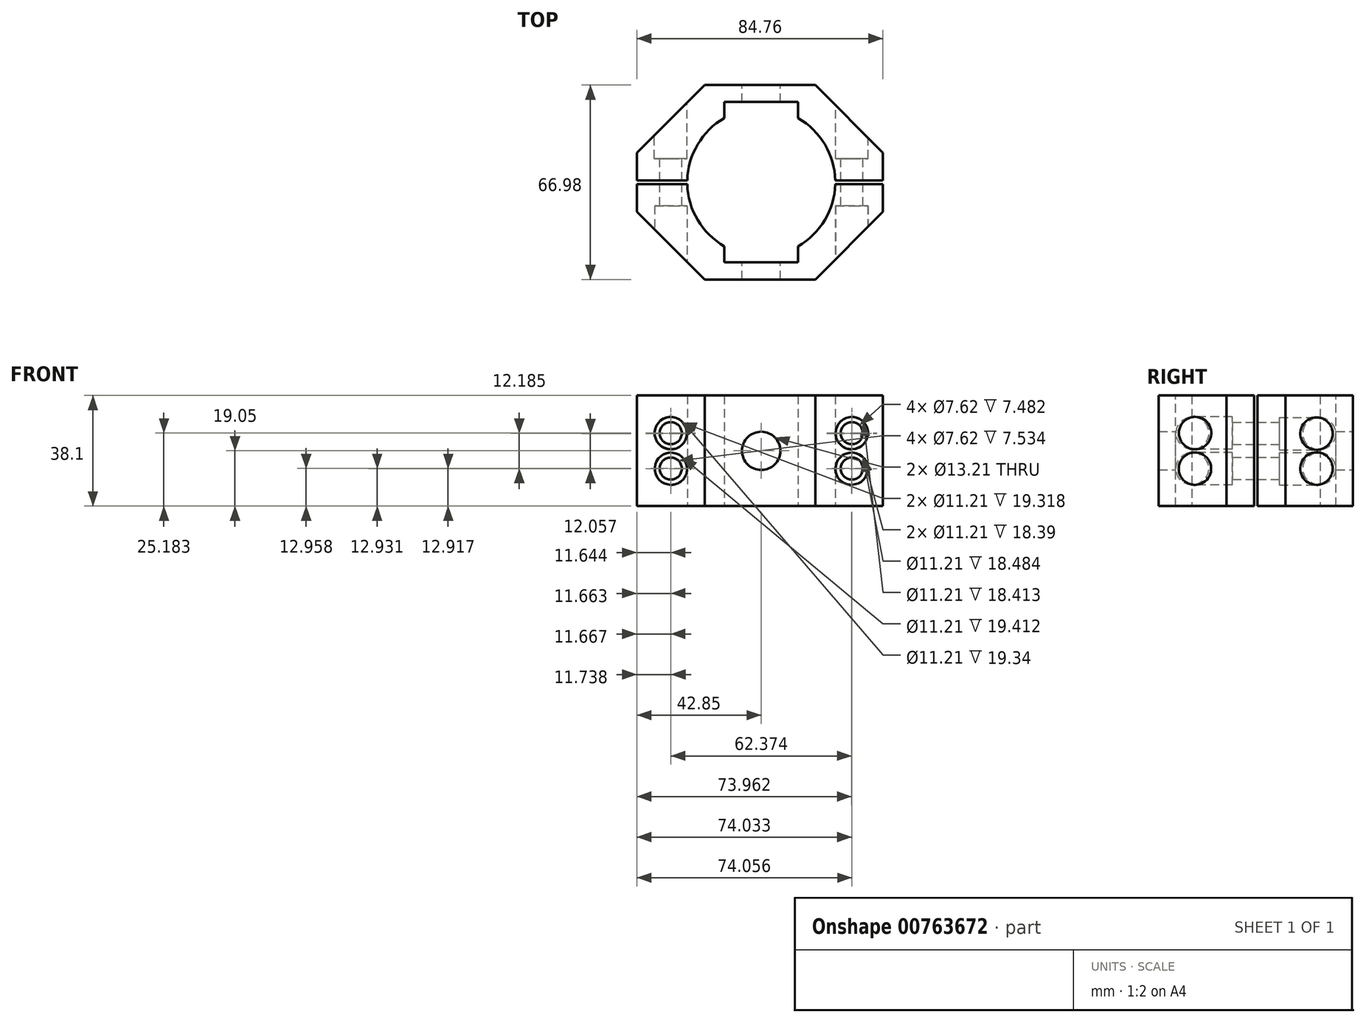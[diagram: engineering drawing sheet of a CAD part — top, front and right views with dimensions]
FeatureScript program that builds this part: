
annotation { "Feature Type Name" : "Feature", "Feature Type Description" : "" }
export const myFeature = defineFeature(function(context is Context, id is Id, definition is map)
    precondition{}
    {
        {
            var Q0;
            Q0=qCreatedBy(makeId("Top.planeOp"),FACE);
            var sketch = newSketch(context, id + "F0", { "sketchPlane" : qUnion([Q0])});
            skLineSegment(sketch, "E0", {"start": v(18.59, 33.5) * mm, "end": v(52.08, 0) * mm});
            skLineSegment(sketch, "E1", {"start": v(52.08, 0) * mm, "end": v(18.59, -33.5) * mm});
            skLineSegment(sketch, "E2", {"start": v(18.59, -33.5) * mm, "end": v(-19.51, -33.5) * mm});
            skLineSegment(sketch, "E3", {"start": v(-19.51, -33.5) * mm, "end": v(-53, 0) * mm});
            skLineSegment(sketch, "E4", {"start": v(-53, 0) * mm, "end": v(-19.51, 33.5) * mm});
            skCircle(sketch, "E5", {"center": v(0, 0) * mm, "radius": 25.48 * mm});
            skLineSegment(sketch, "E6", {"start": v(-19.51, 33.5) * mm, "end": v(18.59, 33.5) * mm});
            skLineSegment(sketch, "E7", {"start": v(0, 33.5) * mm, "end": v(0, 0) * mm});
            skLineSegment(sketch, "E8.bottom", {"start": v(-56.04, 16.89) * mm, "end": v(-42.85, 16.89) * mm});
            skLineSegment(sketch, "E8.top", {"start": v(-56.04, -17.81) * mm, "end": v(-42.85, -17.81) * mm});
            skLineSegment(sketch, "E8.left", {"start": v(-56.04, 16.89) * mm, "end": v(-56.04, -17.81) * mm});
            skLineSegment(sketch, "E8.right", {"start": v(-42.85, 16.89) * mm, "end": v(-42.85, -17.81) * mm});
            skLineSegment(sketch, "E9.left", {"start": v(41.9, 16.59) * mm, "end": v(41.9, -18.11) * mm});
            skLineSegment(sketch, "E9.bottom", {"start": v(41.9, 16.59) * mm, "end": v(54.8, 16.59) * mm});
            skLineSegment(sketch, "E9.right", {"start": v(54.8, 16.59) * mm, "end": v(54.8, -18.11) * mm});
            skLineSegment(sketch, "E9.top", {"start": v(41.9, -18.11) * mm, "end": v(54.8, -18.11) * mm});
            skLineSegment(sketch, "E10", {"start": v(-53, 0) * mm, "end": v(-42.85, 0) * mm});
            skLineSegment(sketch, "E11", {"start": v(41.92, 0) * mm, "end": v(52.08, 0) * mm});
            skSolve(sketch);
        }
        {
            var Q0;
            {var subQ13=sQuery(id+"F0.wireOp",EDGE,"E2");Q0=makeQuery(id+"F0.imprint","IMPRINT",FACE,{"disambiguationData":[TD([[makeQuery(id+"F0.imprint","IMPRINT",EDGE,{"derivedFrom":subQ13}),-1.0]])]});}
            extrude(context, id + "F1", {"entities" : qUnion([Q0]), "endBound" : BoundingType.SYMMETRIC, "depth" : 38.1 * mm});
        }
        {
            var Q0;
            Q0=makeQuery(id+"F1.opExtrude","SWEPT_FACE",FACE,{"disambiguationData":[OSD([sQuery(id+"F0.wireOp",EDGE,"E6")])]});
            var sketch = newSketch(context, id + "F2", { "sketchPlane" : qUnion([Q0])});
            skCircle(sketch, "E12.MirrorC", {"center": v(31.19, 6.1) * mm, "radius": 3.81 * mm});
            skCircle(sketch, "E13", {"center": v(-31.19, 6.1) * mm, "radius": 3.81 * mm});
            skCircle(sketch, "E14", {"center": v(-31.19, -6.1) * mm, "radius": 3.81 * mm});
            skCircle(sketch, "E15.MirrorC", {"center": v(31.19, -6.1) * mm, "radius": 3.81 * mm});
            skLineSegment(sketch, "E16", {"start": v(-31.19, 6.1) * mm, "end": v(-31.19, -6.1) * mm});
            skLineSegment(sketch, "E17", {"start": v(31.19, 6.1) * mm, "end": v(31.19, -6.1) * mm});
            skCircle(sketch, "E18", {"center": v(0, 0) * mm, "radius": 6.6 * mm});
            skLineSegment(sketch, "E19", {"start": v(31.19, 0) * mm, "end": v(-31.19, 0) * mm});
            skSolve(sketch);
        }
        {
            var Q0;
            Q0=qSketchRegion(id+"F2",true);
            extrude(context, id + "F3", {"entities" : qUnion([Q0]), "operationType" : NewBodyOperationType.REMOVE, "endBound" : BoundingType.THROUGH_ALL, "oppositeDirection" : true, "depth" : 25.4 * mm});
        }
        {
            var Q0;
            Q0=makeQuery(id+"F1.opExtrude","SWEPT_FACE",FACE,{"disambiguationData":[OSD([sQuery(id+"F0.wireOp",EDGE,"E2")])]});
            var sketch = newSketch(context, id + "F4", { "sketchPlane" : qUnion([Q0])});
            skCircle(sketch, "E20", {"center": v(-31.18, 6.13) * mm, "radius": 5.6 * mm});
            skCircle(sketch, "E21", {"center": v(-31.11, -6.13) * mm, "radius": 5.6 * mm});
            skLineSegment(sketch, "E22", {"start": v(-31.18, 6.13) * mm, "end": v(-31.11, -6.13) * mm});
            skLineSegment(sketch, "E23", {"start": v(-31.15, 0) * mm, "end": v(18.59, 0) * mm});
            skCircle(sketch, "E24.MirrorC", {"center": v(31.11, -6.13) * mm, "radius": 5.6 * mm});
            skCircle(sketch, "E25.MirrorC", {"center": v(31.18, 6.13) * mm, "radius": 5.6 * mm});
            skSolve(sketch);
        }
        {
            var Q0;
            Q0=qSketchRegion(id+"F4",true);
            extrude(context, id + "F5", {"entities" : qUnion([Q0]), "operationType" : NewBodyOperationType.REMOVE, "oppositeDirection" : true, "depth" : 25.4 * mm});
        }
        {
            var Q0;
            Q0=makeQuery(id+"F1.opExtrude","SWEPT_FACE",FACE,{"disambiguationData":[OSD([sQuery(id+"F0.wireOp",EDGE,"E6")])]});
            var sketch = newSketch(context, id + "F6", { "sketchPlane" : qUnion([Q0])});
            skCircle(sketch, "E26", {"center": v(-31.2, 5.94) * mm, "radius": 5.6 * mm});
            skCircle(sketch, "E27", {"center": v(-31.2, -6.12) * mm, "radius": 5.6 * mm});
            skLineSegment(sketch, "E28", {"start": v(-31.2, 5.94) * mm, "end": v(-31.2, -6.12) * mm});
            skCircle(sketch, "E29.MirrorC", {"center": v(31.2, 5.94) * mm, "radius": 5.6 * mm});
            skCircle(sketch, "E30.MirrorC", {"center": v(31.2, -6.12) * mm, "radius": 5.6 * mm});
            skLineSegment(sketch, "E31", {"start": v(31.2, 5.94) * mm, "end": v(31.2, -6.12) * mm});
            skLineSegment(sketch, "E32", {"start": v(31.2, -0.09) * mm, "end": v(-31.2, -0.09) * mm});
            skSolve(sketch);
        }
        {
            var Q0;
            Q0=qSketchRegion(id+"F6",true);
            extrude(context, id + "F7", {"entities" : qUnion([Q0]), "operationType" : NewBodyOperationType.REMOVE, "oppositeDirection" : true, "depth" : 25.4 * mm});
        }
        {
            var Q0;
            Q0=makeQuery(id+"F1.opExtrude","CAP_FACE",FACE,{"disambiguationData":[OSD([sQuery(id+"F0.wireOp",EDGE,"E0"),sQuery(id+"F0.wireOp",EDGE,"E1"),sQuery(id+"F0.wireOp",EDGE,"E2"),sQuery(id+"F0.wireOp",EDGE,"E3"),sQuery(id+"F0.wireOp",EDGE,"E4"),sQuery(id+"F0.wireOp",EDGE,"E5"),sQuery(id+"F0.wireOp",EDGE,"E6"),sQuery(id+"F0.wireOp",EDGE,"E8.right"),sQuery(id+"F0.wireOp",EDGE,"E9.left")])],"isStart":true});
            var sketch = newSketch(context, id + "F8", { "sketchPlane" : qUnion([Q0])});
            skLineSegment(sketch, "E33.bottom", {"start": v(-49.62, 0.61) * mm, "end": v(60.64, 0.61) * mm});
            skLineSegment(sketch, "E33.top", {"start": v(-49.62, -0.56) * mm, "end": v(60.64, -0.56) * mm});
            skLineSegment(sketch, "E33.left", {"start": v(-49.62, 0.61) * mm, "end": v(-49.62, -0.56) * mm});
            skLineSegment(sketch, "E33.right", {"start": v(60.64, 0.61) * mm, "end": v(60.64, -0.56) * mm});
            skSolve(sketch);
        }
        {
            var Q0;
            Q0=qSketchRegion(id+"F8",true);
            extrude(context, id + "F9", {"entities" : qUnion([Q0]), "operationType" : NewBodyOperationType.REMOVE, "endBound" : BoundingType.THROUGH_ALL, "oppositeDirection" : true, "depth" : 83.51 * mm});
        }
        {
            var Q0;
            {var subQ0=sQuery(id+"F0.wireOp",EDGE,"E6");var subQ1=sQuery(id+"F0.wireOp",EDGE,"E5");var subQ2=sQuery(id+"F0.wireOp",EDGE,"E4");var subQ3=sQuery(id+"F0.wireOp",EDGE,"E0");var subQ4=sQuery(id+"F0.wireOp",EDGE,"E8.right");var subQ5=sQuery(id+"F0.wireOp",EDGE,"E9.left");Q0=makeQuery(id+"F9.boolean.opBoolean","SPLIT",FACE,{"disambiguationData":[TD([makeQuery(id+"F1.opExtrude","SWEPT_FACE",FACE,{"disambiguationData":[OSD([subQ3])]})])],"derivedFrom":makeQuery(id+"F1.opExtrude","CAP_FACE",FACE,{"disambiguationData":[OSD([subQ3,sQuery(id+"F0.wireOp",EDGE,"E1"),sQuery(id+"F0.wireOp",EDGE,"E2"),sQuery(id+"F0.wireOp",EDGE,"E3"),subQ2,subQ1,subQ0,subQ4,subQ5])],"isStart":false})});}
            var sketch = newSketch(context, id + "F10", { "sketchPlane" : qUnion([Q0])});
            skLineSegment(sketch, "E34.bottom", {"start": v(-12.7, -21.31) * mm, "end": v(12.7, -21.31) * mm});
            skLineSegment(sketch, "E34.top", {"start": v(-12.7, -27.61) * mm, "end": v(12.7, -27.61) * mm});
            skLineSegment(sketch, "E34.left", {"start": v(-12.7, -21.31) * mm, "end": v(-12.7, -27.61) * mm});
            skLineSegment(sketch, "E34.right", {"start": v(12.7, -21.31) * mm, "end": v(12.7, -27.61) * mm});
            skLineSegment(sketch, "E35", {"start": v(0, 0) * mm, "end": v(0, -21.31) * mm});
            skLineSegment(sketch, "E36.MirrorCS", {"start": v(-12.7, 21.31) * mm, "end": v(12.7, 21.31) * mm});
            skLineSegment(sketch, "E37.MirrorCS", {"start": v(-12.7, 21.31) * mm, "end": v(-12.7, 27.61) * mm});
            skLineSegment(sketch, "E38.MirrorCS", {"start": v(12.7, 21.31) * mm, "end": v(12.7, 27.61) * mm});
            skLineSegment(sketch, "E39.MirrorCS", {"start": v(-12.7, 27.61) * mm, "end": v(12.7, 27.61) * mm});
            skSolve(sketch);
        }
        {
            var Q0;
            Q0=qSketchRegion(id+"F10",true);
            extrude(context, id + "F11", {"entities" : qUnion([Q0]), "operationType" : NewBodyOperationType.REMOVE, "endBound" : BoundingType.THROUGH_ALL, "oppositeDirection" : true, "depth" : 25.4 * mm});
        }
        {
            var Q0;
            Q0=makeQuery(id+"F1.opExtrude","SWEPT_FACE",FACE,{"disambiguationData":[OSD([sQuery(id+"F0.wireOp",EDGE,"E6")])]});
            cPlane(context, id + "F12", {"entities" : qUnion([Q0]), "cplaneType" : CPlaneType.OFFSET, "offset" : 0 * mm, "width" : 152.4 * mm, "height" : 152.4 * mm});
        }
    });
